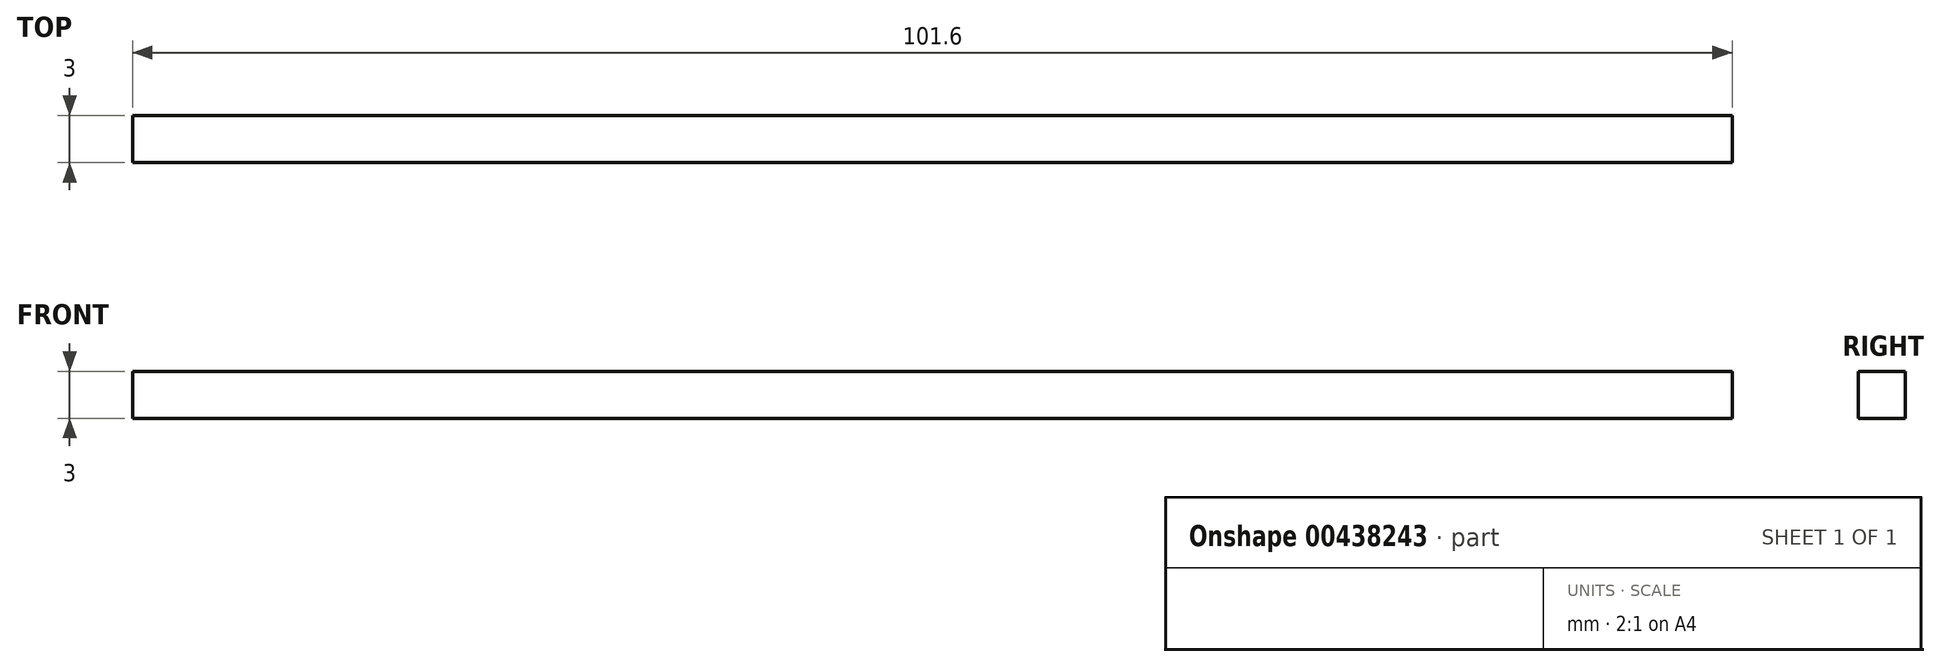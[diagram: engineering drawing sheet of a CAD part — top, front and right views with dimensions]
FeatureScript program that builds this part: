
annotation { "Feature Type Name" : "Feature", "Feature Type Description" : "" }
export const myFeature = defineFeature(function(context is Context, id is Id, definition is map)
    precondition{}
    {
        {
            var Q0;
            Q0=qCreatedBy(makeId("Front.planeOp"),FACE);
            var sketch = newSketch(context, id + "F0", { "sketchPlane" : qUnion([Q0])});
            skLineSegment(sketch, "E0.bottom", {"start": v(-56.5, 13.06) * mm, "end": v(45.1, 13.06) * mm});
            skLineSegment(sketch, "E0.top", {"start": v(-56.5, 16.06) * mm, "end": v(45.1, 16.06) * mm});
            skLineSegment(sketch, "E0.left", {"start": v(-56.5, 13.06) * mm, "end": v(-56.5, 16.06) * mm});
            skLineSegment(sketch, "E0.right", {"start": v(45.1, 13.06) * mm, "end": v(45.1, 16.06) * mm});
            skSolve(sketch);
        }
        {
            var Q0;
            Q0=makeQuery(id+"F0.imprint","IMPRINT",FACE,{"disambiguationData":[TD([[makeQuery(id+"F0.imprint","IMPRINT",EDGE,{"derivedFrom":sQuery(id+"F0.wireOp",EDGE,"E0.bottom")}),1.0]])]});
            extrude(context, id + "F1", {"entities" : qUnion([Q0]), "depth" : 3 * mm});
        }
    });
